# Revit family: Zumtobel CR2P MOUNTING FRAME
name_source: partatom
category: Lighting Fixtures
revit_build: Autodesk Revit 2016 (Build: 20150220_1215(x64)
units: mm (PartAtom-declared; Revit-internal decimal feet)

## family parameters
Cut with Voids When Loaded = No
Host = Face
Light Source = No
OmniClass Number = 23.80.70.11
OmniClass Title = Luminaries for Internal Lighting
Part Type = Normal
Room Calculation Point = No
Round Connector Dimension = Use Diameter
Shared = No

## types (2) — shared parameters
Apparent Load = 0 VA
Assembly Code = D5020200
Body = ZG_Metal_White
Lamp = LED
Manufacturer = Zumtobel Lighting
zero-valued in all types: Default Elevation

## per-type parameters (varying)
| type | Description | Height | Length | Model | URL | Width |
| CR2PL M MOUNTING FRAME | CR2PL M Mounting Frame | 109 mm | 650 mm | 22171570 | www.zumtobel.com/22171570 | 540 mm |
| CR2 M MOUNTING FRAME | CR2 M Mounting Frame | 83 mm  [stored 0.27231 ft] | 670 mm  [stored 2.19816 ft] | 22171572 | www.zumtobel.com/22171572 | 600 mm |

note: [stored X ft] marks values corroborated as IEEE doubles in the binary element streams (Revit-internal decimal feet)

## geometry (parser evidence)
native form markers: Blend x2, Sweep x4
no freeform markers — native parametric forms only
